# Revit family: 2M_Butterfly Valve_UNIVAL_BWN-0302 - 40-600 mm
name_source: partatom
category: Pipe Accessories
revit_build: Autodesk Revit 2016 (Build: 20150220_1215(x64)
units: mm (PartAtom-declared; Revit-internal decimal feet)

## family parameters
Always vertical = Yes
Cut with Voids When Loaded = No
OmniClass Number = 23.65.55.14.17
OmniClass Title = Adjusting/Controlling Valves for Liquid Services
Part Type = Valve - Breaks Into
Round Connector Dimension = Use Diameter
Shared = No
Work Plane-Based = No

## types (15) — shared parameters
Body Material = Ductile iron
Certifications = TSE EAC CE
Connection Type = Wafer
Description = Wafer type butterfly valve
Description TR = Wafer tip kelebek vana
Disc Material = Nickel plated ductile iron
Gasket Material = EPDM / NBR
K Coefficient Table = Butterfly Valve Full Open
Loss Method = K Coefficient from Table
Manufacturer = Giacomini Unival
Giacomini Unival
Max. Working Pressure = 11 Bar
Max. Working Temperature = EPDM 120°C (water), NBR 90°C (water and petroleum oil)
Pressure Rating = PN16
Seat Material = EPDM / NBR
Standard No = TS EN 593+A1
URL = http://www.unival.com.tr

## per-type parameters (varying)
| type | A | B | Body_r | D | DN | Disc_r | E | EarBottom_h | EarEdge_r | Ear_x1 | Ear_y1 | Eclipse_angle | Eclipse_h | Eclipse_l | Eclipse_r1 | Eclipse_r2 | Kv | Max Diff. Pressure (Allowed) | Model | Operator Type | Stem_D | Stem_top_h | T |
| DN100 | 180 mm | 100 mm | 73 mm | 90 mm | 100 mm | 50 mm  [stored 0.164042 ft] | 52 mm | 90 mm | 25 mm  [stored 0.082021 ft] | 32 mm  [stored 0.104987 ft] | 40 mm  [stored 0.131234 ft] | 30.00° | 86 mm | 36 mm  [stored 0.11811 ft] | 26 mm | 20 mm  [stored 0.0656168 ft] | 760 | 3 Bar | BWN-0302X100 | M_Handle - Curved : Lever_260mm | 35 mm  [stored 0.114829 ft] | 1 mm  [stored 0.00328084 ft] | -10 mm  [stored -0.0328084 ft] |
| DN250 | 274 mm | 200 mm | 148 mm | 125 mm | 250 mm | 125 mm | 69 mm | 180 mm | 32 mm  [stored 0.104987 ft] | 75 mm | 70 mm | 30.00° | 168 mm | 70 mm | 52 mm | 40 mm  [stored 0.131234 ft] | 5050 | 1.5 Bar | BWN-0302X250 | M_Handle - Curved : Lever_416mm | 46 mm  [stored 0.150919 ft] | 26 mm | -10 mm  [stored -0.0328084 ft] |
| DN40 | 140 mm | 64 mm | 43 mm  [stored 0.141076 ft] | 90 mm | 40 mm | 20 mm  [stored 0.0656168 ft] | 35 mm  [stored 0.114829 ft] | 54 mm  [stored 0.177165 ft] | 10 mm  [stored 0.0328084 ft] | 20 mm  [stored 0.0656168 ft] | 22 mm  [stored 0.0721785 ft] | 20.00° | 50 mm  [stored 0.164042 ft] | 20 mm  [stored 0.0656168 ft] | 18 mm  [stored 0.0590551 ft] | 14 mm  [stored 0.0459318 ft] | 49.5 | 3 Bar | BWN-0302X040 | M_Handle - Curved : Lever_260mm | 23 mm  [stored 0.0754593 ft] | 1 mm  [stored 0.00328084 ft] | -10 mm  [stored -0.0328084 ft] |
| DN50 | 140 mm | 69 mm | 48 mm  [stored 0.15748 ft] | 90 mm | 50 mm | 25 mm  [stored 0.082021 ft] | 43 mm  [stored 0.141076 ft] | 60 mm | 14 mm  [stored 0.0459318 ft] | 20 mm  [stored 0.0656168 ft] | 22 mm  [stored 0.0721785 ft] | 30.00° | 56 mm  [stored 0.183727 ft] | 22 mm  [stored 0.0721785 ft] | 18 mm  [stored 0.0590551 ft] | 14 mm  [stored 0.0459318 ft] | 115 | 3 Bar | BWN-0302X050 | M_Handle - Curved : Lever_260mm | 29 mm | 1 mm  [stored 0.00328084 ft] | -10 mm  [stored -0.0328084 ft] |
| DN65 | 152 mm | 76 mm | 56 mm  [stored 0.183727 ft] | 90 mm | 65 mm | 33 mm | 45 mm  [stored 0.147638 ft] | 70 mm | 14 mm  [stored 0.0459318 ft] | 20 mm  [stored 0.0656168 ft] | 22 mm  [stored 0.0721785 ft] | 30.00° | 65 mm | 23 mm  [stored 0.0754593 ft] | 18 mm  [stored 0.0590551 ft] | 14 mm  [stored 0.0459318 ft] | 255 | 3 Bar | BWN-0302X065 | M_Handle - Curved : Lever_260mm | 30 mm  [stored 0.0984252 ft] | 1 mm  [stored 0.00328084 ft] | -10 mm  [stored -0.0328084 ft] |
| DN80 | 160 mm | 85 mm | 63 mm | 90 mm | 80 mm | 40 mm  [stored 0.131234 ft] | 46 mm  [stored 0.150919 ft] | 75 mm | 20 mm  [stored 0.0656168 ft] | 22 mm  [stored 0.0721785 ft] | 22 mm  [stored 0.0721785 ft] | 30.00° | 70 mm | 27 mm  [stored 0.0885827 ft] | 20 mm  [stored 0.0656168 ft] | 15 mm  [stored 0.0492126 ft] | 375 | 3 Bar | BWN-0302X080 | M_Handle - Curved : Lever_260mm | 31 mm | 1 mm  [stored 0.00328084 ft] | -10 mm  [stored -0.0328084 ft] |
| DN125 | 191 mm | 120 mm | 86 mm | 90 mm | 125 mm | 63 mm | 56 mm  [stored 0.183727 ft] | 105 mm | 28 mm  [stored 0.0918635 ft] | 34 mm | 36 mm  [stored 0.11811 ft] | 30.00° | 98 mm | 38 mm  [stored 0.124672 ft] | 28 mm  [stored 0.0918635 ft] | 22 mm  [stored 0.0721785 ft] | 1030 | 3 Bar | BWN-0302X125 | M_Handle - Curved : Lever_260mm | 38 mm  [stored 0.124672 ft] | 1 mm  [stored 0.00328084 ft] | -10 mm  [stored -0.0328084 ft] |
| DN150 | 202 mm | 132 mm | 98 mm | 90 mm | 150 mm | 75 mm | 57 mm | 117 mm | 25 mm  [stored 0.082021 ft] | 42 mm  [stored 0.137795 ft] | 42 mm  [stored 0.137795 ft] | 30.00° | 110 mm | 46 mm  [stored 0.150919 ft] | 30 mm  [stored 0.0984252 ft] | 23 mm  [stored 0.0754593 ft] | 1790 | 3 Bar | BWN-0302X150 | M_Handle - Curved : Lever_260mm | 38 mm  [stored 0.124672 ft] | 1 mm  [stored 0.00328084 ft] | -10 mm  [stored -0.0328084 ft] |
| DN200 | 237 mm | 160 mm | 123 mm | 125 mm | 200 mm | 100 mm | 60 mm | 145 mm | 30 mm  [stored 0.0984252 ft] | 56 mm  [stored 0.183727 ft] | 52 mm | 30.00° | 136 mm | 58 mm | 42 mm  [stored 0.137795 ft] | 32 mm  [stored 0.104987 ft] | 3450 | 3 Bar | BWN-0302X200 | M_Handle - Curved : Lever_326mm | 40 mm  [stored 0.131234 ft] | 23 mm  [stored 0.0754593 ft] | -10 mm  [stored -0.0328084 ft] |
| DN300 | 312 mm | 230 mm | 173 mm | 125 mm | 300 mm | 150 mm | 80 mm | 208 mm | 40 mm  [stored 0.131234 ft] | 80 mm | 80 mm | 30.00° | 194 mm | 84 mm | 58 mm | 45 mm  [stored 0.147638 ft] | 7420 | 1.5 Bar | BWN-0302X300 | M_Handle - Curved : Lever_416mm | 53 mm  [stored 0.173885 ft] | 26 mm | -10 mm  [stored -0.0328084 ft] |
| DN350 | 368 mm | 280 mm | 198 mm | 125 mm | 350 mm | 175 mm | 78 mm | 270 mm | 44 mm  [stored 0.144357 ft] | 86 mm | 90 mm | 30.00° | 228 mm | 78 mm | 70 mm | 54 mm  [stored 0.177165 ft] | 10300 |  | BWN-0302X350 | M_Gear - Operator  : GearS | 52 mm | 1 mm  [stored 0.00328084 ft] | -24 mm  [stored -0.0787402 ft] |
| DN400 | 400 mm | 310 mm | 223 mm | 175 mm | 400 mm | 200 mm | 88 mm | 300 mm | 44 mm  [stored 0.144357 ft] | 94 mm | 90 mm | 30.00° | 256 mm | 84 mm | 74 mm | 57 mm | 14007 |  | BWN-0302X400 | M_Gear - Operator  : GearM | 59 mm | 1 mm  [stored 0.00328084 ft] | -25 mm  [stored -0.082021 ft] |
| DN450 | 422 mm | 340 mm | 248 mm | 175 mm | 450 mm | 225 mm | 109 mm | 330 mm | 44 mm  [stored 0.144357 ft] | 94 mm | 90 mm | 30.00° | 280 mm | 86 mm | 74 mm | 57 mm | 18551 |  | BWN-0302X450 | M_Gear - Operator  : GearM | 73 mm | 1 mm  [stored 0.00328084 ft] | -26 mm |
| DN500 | 480 mm | 388 mm | 273 mm | 210 mm | 500 mm | 250 mm | 127 mm | 370 mm | 50 mm  [stored 0.164042 ft] | 110 mm | 96 mm | 30.00° | 310 mm | 100 mm | 84 mm | 65 mm | 23853 |  | BWN-0302X500 | M_Gear - Operator  : GearL | 85 mm | 1 mm  [stored 0.00328084 ft] | -25 mm  [stored -0.082021 ft] |
| DN600 | 562 mm | 450 mm | 323 mm | 210 mm | 600 mm | 300 mm | 154 mm | 436 mm | 50 mm  [stored 0.164042 ft] | 130 mm | 130 mm | 30.00° | 376 mm | 116 mm | 100 mm | 77 mm | 36894 |  | BWN-0302X600 | M_Gear - Operator  : GearL | 103 mm | 1 mm  [stored 0.00328084 ft] | -30 mm  [stored -0.0984252 ft] |

note: [stored X ft] marks values corroborated as IEEE doubles in the binary element streams (Revit-internal decimal feet)

## geometry (parser evidence)
native form markers: Sweep x6
no freeform markers — native parametric forms only
